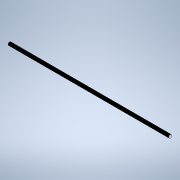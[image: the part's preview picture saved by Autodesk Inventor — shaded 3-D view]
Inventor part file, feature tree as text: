
AUTODESK INVENTOR PART (.ipt)
format: ipt  version: 2020 (Build 240168000, 168)  size: 93,184 bytes
history: native  units: mm
features: extrude x1, sketch x1
ambient origin geometry x8: Origin, YZ Plane, XZ Plane, XY Plane, X Axis, Y Axis, Z Axis, Center Point
bodies: Solid1 (feature_tree)
feature tree (2):
  extrude  "Extrusion1"  Depth=400.0mm TaperAngle=0.0deg
  sketch  "Sketch1"  dims[d0=8.0mm d1=400.0mm d2=0.0mm]
